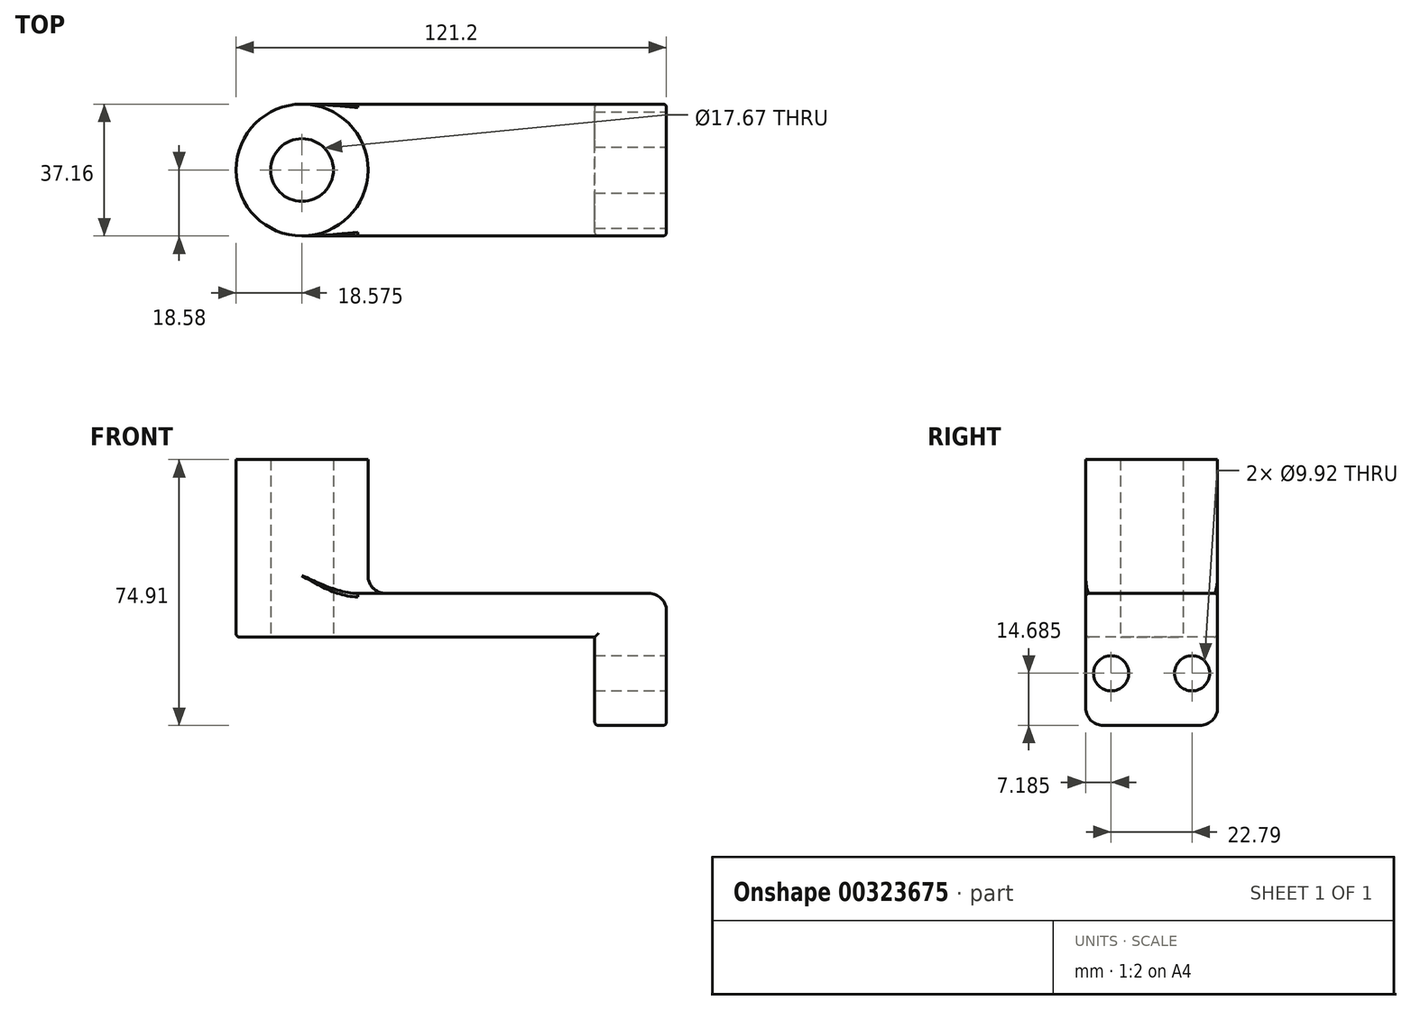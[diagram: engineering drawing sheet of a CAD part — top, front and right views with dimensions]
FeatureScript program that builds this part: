
annotation { "Feature Type Name" : "Feature", "Feature Type Description" : "" }
export const myFeature = defineFeature(function(context is Context, id is Id, definition is map)
    precondition{}
    {
        {
            var Q0;
            Q0=qCreatedBy(makeId("Top.planeOp"),FACE);
            var sketch = newSketch(context, id + "F0", { "sketchPlane" : qUnion([Q0])});
            skLineSegment(sketch, "E0.bottom", {"start": v(51.31, 18.58) * mm, "end": v(-51.31, 18.58) * mm});
            skLineSegment(sketch, "E0.top", {"start": v(51.31, -18.58) * mm, "end": v(-51.31, -18.58) * mm});
            skLineSegment(sketch, "E0.left", {"start": v(51.31, 18.58) * mm, "end": v(51.31, -18.58) * mm});
            skLineSegment(sketch, "E0.right", {"start": v(-51.31, 18.58) * mm, "end": v(-51.31, -18.58) * mm});
            skPoint(sketch, "E0.middle", {"position": v(0, 0) * mm});
            skCircle(sketch, "E1", {"center": v(-51.31, 0) * mm, "radius": 18.58 * mm});
            skCircle(sketch, "E2", {"center": v(-51.31, 0) * mm, "radius": 8.83 * mm});
            skSolve(sketch);
        }
        {
            var Q0;
            {var subQ0=sQuery(id+"F0.wireOp",EDGE,"E0.bottom");Q0=makeQuery(id+"F0.imprint","IMPRINT",FACE,{"disambiguationData":[TD([[makeQuery(id+"F0.imprint","IMPRINT",EDGE,{"derivedFrom":subQ0}),1.0]])]});}
            var Q1;
            {var subQ1=sQuery(id+"F0.wireOp",EDGE,"E0.right");var subQ3=sQuery(id+"F0.wireOp",EDGE,"E2");var subQ4=makeQuery(id+"F0.imprint","INTERSECT",VERTEX,{"disambiguationData":[OD(0.0)],"derivedFrom":[subQ1,subQ3]});Q1=makeQuery(id+"F0.imprint","IMPRINT",FACE,{"disambiguationData":[TD([[makeQuery(id+"F0.imprint","IMPRINT",EDGE,{"disambiguationData":[TD([[subQ4,-1.0]])],"derivedFrom":subQ3}),-1.0]])]});}
            var Q2;
            {var subQ1=sQuery(id+"F0.wireOp",EDGE,"E0.right");var subQ3=sQuery(id+"F0.wireOp",EDGE,"E2");var subQ4=makeQuery(id+"F0.imprint","INTERSECT",VERTEX,{"disambiguationData":[OD(0.0)],"derivedFrom":[subQ1,subQ3]});Q2=makeQuery(id+"F0.imprint","IMPRINT",FACE,{"disambiguationData":[TD([[makeQuery(id+"F0.imprint","IMPRINT",EDGE,{"disambiguationData":[TD([[subQ4,1.0]])],"derivedFrom":subQ3}),-1.0]])]});}
            extrude(context, id + "F1", {"entities" : qUnion([Q0, Q1, Q2]), "depth" : 12.3 * mm});
        }
        {
            var Q0;
            {var subQ1=sQuery(id+"F0.wireOp",EDGE,"E0.right");var subQ3=sQuery(id+"F0.wireOp",EDGE,"E2");var subQ4=makeQuery(id+"F0.imprint","INTERSECT",VERTEX,{"disambiguationData":[OD(0.0)],"derivedFrom":[subQ1,subQ3]});Q0=makeQuery(id+"F0.imprint","IMPRINT",FACE,{"disambiguationData":[TD([[makeQuery(id+"F0.imprint","IMPRINT",EDGE,{"disambiguationData":[TD([[subQ4,1.0]])],"derivedFrom":subQ3}),-1.0]])]});}
            var Q1;
            {var subQ1=sQuery(id+"F0.wireOp",EDGE,"E0.right");var subQ3=sQuery(id+"F0.wireOp",EDGE,"E2");var subQ4=makeQuery(id+"F0.imprint","INTERSECT",VERTEX,{"disambiguationData":[OD(0.0)],"derivedFrom":[subQ1,subQ3]});Q1=makeQuery(id+"F0.imprint","IMPRINT",FACE,{"disambiguationData":[TD([[makeQuery(id+"F0.imprint","IMPRINT",EDGE,{"disambiguationData":[TD([[subQ4,-1.0]])],"derivedFrom":subQ3}),-1.0]])]});}
            extrude(context, id + "F2", {"entities" : qUnion([Q0, Q1]), "operationType" : NewBodyOperationType.ADD, "depth" : 50 * mm});
        }
        {
            var Q0;
            Q0=makeQuery(id+"F1.opExtrude","SWEPT_FACE",FACE,{"disambiguationData":[OSD([sQuery(id+"F0.wireOp",EDGE,"E0.left")])]});
            var sketch = newSketch(context, id + "F3", { "sketchPlane" : qUnion([Q0])});
            skLineSegment(sketch, "E3.bottom", {"start": v(-18.58, 12.3) * mm, "end": v(18.58, 12.3) * mm});
            skLineSegment(sketch, "E3.top", {"start": v(-18.58, -24.91) * mm, "end": v(18.58, -24.91) * mm});
            skLineSegment(sketch, "E3.left", {"start": v(-18.58, 12.3) * mm, "end": v(-18.58, -24.91) * mm});
            skLineSegment(sketch, "E3.right", {"start": v(18.58, 12.3) * mm, "end": v(18.58, -24.91) * mm});
            skCircle(sketch, "E4", {"center": v(-11.4, -10.22) * mm, "radius": 4.96 * mm});
            skLineSegment(sketch, "E5", {"start": v(0, 0) * mm, "end": v(0, -24.91) * mm, "construction": true});
            skCircle(sketch, "E6.MirrorC", {"center": v(11.4, -10.22) * mm, "radius": 4.96 * mm});
            skSolve(sketch);
        }
        {
            var Q0;
            {var subQ2=sQuery(id+"F3.wireOp",EDGE,"E3.top");Q0=makeQuery(id+"F3.imprint","IMPRINT",FACE,{"disambiguationData":[TD([[makeQuery(id+"F3.imprint","IMPRINT",EDGE,{"derivedFrom":subQ2}),1.0]])]});}
            extrude(context, id + "F4", {"entities" : qUnion([Q0]), "operationType" : NewBodyOperationType.ADD, "oppositeDirection" : true, "depth" : 20.2 * mm});
        }
        {
            var Q0;
            {var subQ0=sQuery(id+"F0.wireOp",EDGE,"E1");Q0=makeQuery(id+"F2.boolean.opBoolean","INTERSECT",EDGE,{"derivedFrom":[makeQuery(id+"F1.opExtrude","CAP_FACE",FACE,{"disambiguationData":[OSD([sQuery(id+"F0.wireOp",EDGE,"E0.bottom"),sQuery(id+"F0.wireOp",EDGE,"E0.top"),sQuery(id+"F0.wireOp",EDGE,"E0.left"),subQ0,sQuery(id+"F0.wireOp",EDGE,"E2")])],"isStart":false}),makeQuery(id+"F2.opExtrude","SWEPT_FACE",FACE,{"disambiguationData":[OSD([subQ0])]})]});}
            var Q1;
            Q1=makeQuery(id+"F1.opExtrude","CAP_EDGE",EDGE,{"disambiguationData":[OSD([sQuery(id+"F0.wireOp",EDGE,"E0.left")])],"isStart":false});
            var Q2;
            Q2=makeQuery(id+"F4.opExtrude","SWEPT_EDGE",EDGE,{"disambiguationData":[OSD([sQuery(id+"F3.wireOp",EDGE,"E3.top"),sQuery(id+"F3.wireOp",EDGE,"E3.right")])]});
            var Q3;
            Q3=makeQuery(id+"F4.opExtrude","SWEPT_EDGE",EDGE,{"disambiguationData":[OSD([sQuery(id+"F3.wireOp",EDGE,"E3.top"),sQuery(id+"F3.wireOp",EDGE,"E3.left")])]});
            fillet(context, id + "F5", {"entities" : qUnion([Q0, Q1, Q2, Q3]), "radius" : 5 * mm, "tangentPropagation" : true, "allowEdgeOverflow" : false});
        }
        {
            var Q0;
            Q0=makeQuery(id+"F1.opExtrude","CAP_EDGE",EDGE,{"disambiguationData":[OSD([sQuery(id+"F0.wireOp",EDGE,"E0.top")])],"isStart":false});
            var Q1;
            Q1=makeQuery(id+"F1.opExtrude","CAP_EDGE",EDGE,{"disambiguationData":[OSD([sQuery(id+"F0.wireOp",EDGE,"E0.top")])],"isStart":true});
            var Q2;
            Q2=makeQuery(id+"F4.opExtrude","CAP_EDGE",EDGE,{"disambiguationData":[OSD([sQuery(id+"F3.wireOp",EDGE,"E3.left")])],"isStart":false});
            fillet(context, id + "F6", {"entities" : qUnion([Q0, Q1, Q2]), "radius" : 1 * mm, "tangentPropagation" : true, "allowEdgeOverflow" : false});
        }
    });
